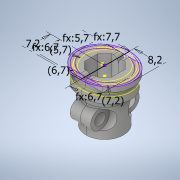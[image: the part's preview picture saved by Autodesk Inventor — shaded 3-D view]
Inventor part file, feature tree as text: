
AUTODESK INVENTOR PART (.ipt)
format: ipt  version: 2021.1 (Build 251245010, 245A)  size: 284,672 bytes
history: mixed  units: in
note: dims shown in document units (in); Inventor stores cm internally (conversion verified against a paired STEP export)
features: extrude x3, other x2, sketch x2, imported_body x1
ambient origin geometry x8: Origin, YZ Plane, XZ Plane, XY Plane, X Axis, Y Axis, Z Axis, Center Point
bodies: Solid1 (imported_parasolid), Solid2 (imported_parasolid)
feature tree (8):
  other  "OBS-D-005"
  sketch  "Skizze1"  dims[d0=0.2638in d1=0.2244in]
  extrude  "Extrusion1"  Depth=0.2244in
  sketch  "Skizze4"  dims[d2=0.2244in d4=0.2835in d5=0.2835in d6=0.3228in d7=0.3937in d8=0.0in d12=0.2638in d13=0.2638in d14=0.3031in d15=0.3937in d16=0.0in d17=0.3937in d18=0.0in]
  extrude  "Extrusion2"  Depth=0.3937in
  extrude  "Extrusion3"  Depth=0.3937in
  other  "OBS-D-004"
  imported_body  NMx_Import_Brep_tag  [imported B-rep: ~74 faces, bbox_mm=[15.4, 15.0, 13.4]]
